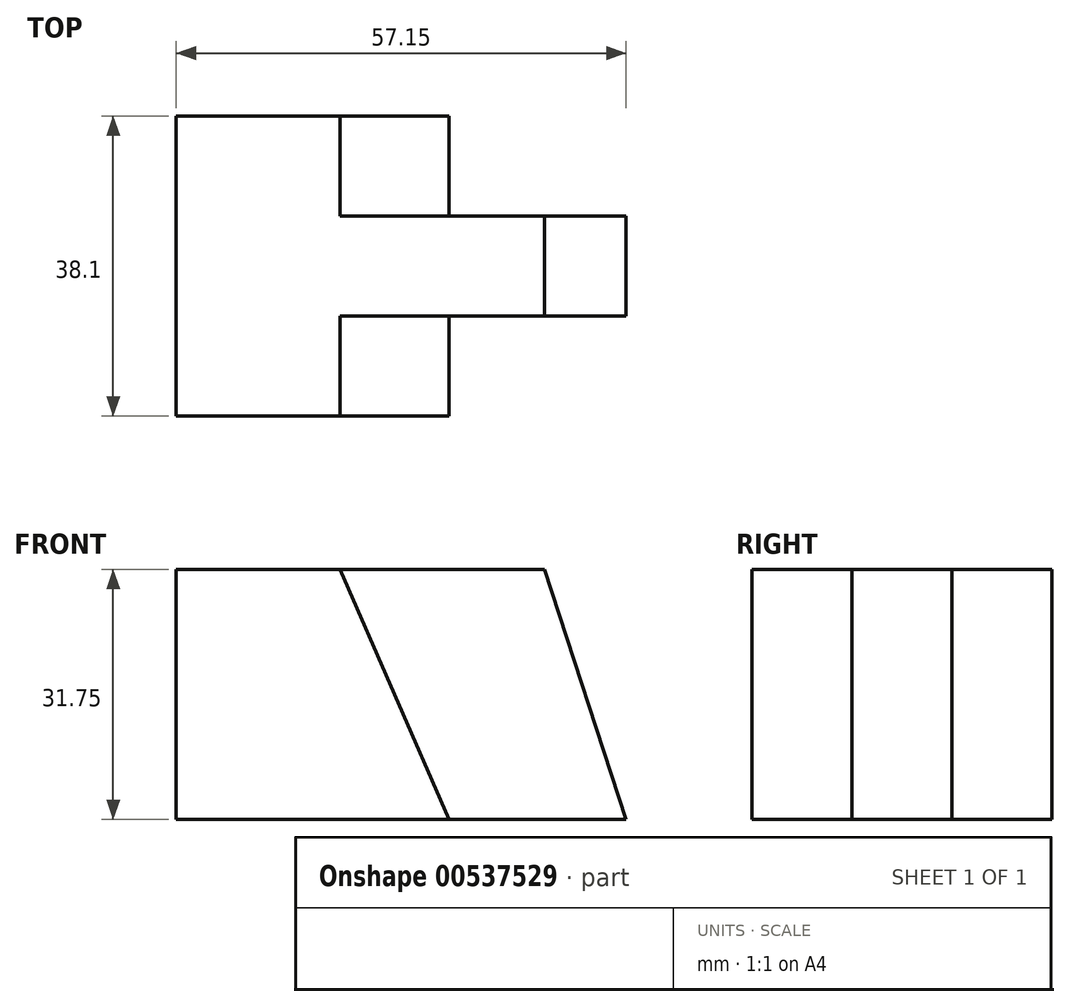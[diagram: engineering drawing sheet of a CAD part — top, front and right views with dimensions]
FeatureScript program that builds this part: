
annotation { "Feature Type Name" : "Feature", "Feature Type Description" : "" }
export const myFeature = defineFeature(function(context is Context, id is Id, definition is map)
    precondition{}
    {
        {
            var Q0;
            Q0=qCreatedBy(makeId("Front.planeOp"),FACE);
            var sketch = newSketch(context, id + "F0", { "sketchPlane" : qUnion([Q0])});
            skLineSegment(sketch, "E0", {"start": v(0, 0) * mm, "end": v(57.15, 0) * mm});
            skLineSegment(sketch, "E1", {"start": v(57.15, 0) * mm, "end": v(57.15, 31.75) * mm});
            skLineSegment(sketch, "E2", {"start": v(57.15, 31.75) * mm, "end": v(0, 31.75) * mm});
            skLineSegment(sketch, "E3", {"start": v(0, 31.75) * mm, "end": v(0, 0) * mm});
            skSolve(sketch);
        }
        {
            var Q0;
            Q0=makeQuery(id+"F0.imprint","IMPRINT",FACE,{"disambiguationData":[TD([[makeQuery(id+"F0.imprint","IMPRINT",EDGE,{"derivedFrom":sQuery(id+"F0.wireOp",EDGE,"E0")}),1.0]])]});
            extrude(context, id + "F1", {"entities" : qUnion([Q0]), "depth" : 38.1 * mm, "offsetDistance" : 25.4 * mm});
        }
        {
            var Q0;
            Q0=makeQuery(id+"F1.opExtrude","CAP_FACE",FACE,{"disambiguationData":[OSD([sQuery(id+"F0.wireOp",EDGE,"E0"),sQuery(id+"F0.wireOp",EDGE,"E1"),sQuery(id+"F0.wireOp",EDGE,"E2"),sQuery(id+"F0.wireOp",EDGE,"E3")])],"isStart":false});
            var sketch = newSketch(context, id + "F2", { "sketchPlane" : qUnion([Q0])});
            skLineSegment(sketch, "E4", {"start": v(20.79, 31.75) * mm, "end": v(34.64, 0) * mm});
            skSolve(sketch);
        }
        {
            var Q0;
            {var subQ0=sQuery(id+"F2.wireOp",EDGE,"E4");Q0=makeQuery(id+"F2.imprint","IMPRINT",FACE,{"disambiguationData":[TD([[makeQuery(id+"F2.imprint","IMPRINT",EDGE,{"derivedFrom":subQ0}),1.0]])]});}
            extrude(context, id + "F3", {"entities" : qUnion([Q0]), "operationType" : NewBodyOperationType.REMOVE, "oppositeDirection" : true, "depth" : 12.7 * mm, "offsetDistance" : 25.4 * mm});
        }
        {
            var Q0;
            Q0=makeQuery(id+"F1.opExtrude","CAP_FACE",FACE,{"disambiguationData":[OSD([sQuery(id+"F0.wireOp",EDGE,"E0"),sQuery(id+"F0.wireOp",EDGE,"E1"),sQuery(id+"F0.wireOp",EDGE,"E2"),sQuery(id+"F0.wireOp",EDGE,"E3")])],"isStart":true});
            var sketch = newSketch(context, id + "F4", { "sketchPlane" : qUnion([Q0])});
            skLineSegment(sketch, "E5", {"start": v(-20.79, 31.75) * mm, "end": v(-34.64, 0) * mm});
            skSolve(sketch);
        }
        {
            var Q0;
            {var subQ0=sQuery(id+"F4.wireOp",EDGE,"E5");Q0=makeQuery(id+"F4.imprint","IMPRINT",FACE,{"disambiguationData":[TD([[makeQuery(id+"F4.imprint","IMPRINT",EDGE,{"derivedFrom":subQ0}),-1.0]])]});}
            extrude(context, id + "F5", {"entities" : qUnion([Q0]), "operationType" : NewBodyOperationType.REMOVE, "oppositeDirection" : true, "depth" : 12.7 * mm, "offsetDistance" : 25.4 * mm});
        }
        {
            var Q0;
            Q0=makeQuery(id+"F3.boolean.opBoolean","COPY",FACE,{"derivedFrom":makeQuery(id+"F3.opExtrude","CAP_FACE",FACE,{"disambiguationData":[OSD([sQuery(id+"F0.wireOp",EDGE,"E0"),sQuery(id+"F0.wireOp",EDGE,"E1"),sQuery(id+"F0.wireOp",EDGE,"E2"),sQuery(id+"F2.wireOp",EDGE,"E4")])],"isStart":false})});
            var sketch = newSketch(context, id + "F6", { "sketchPlane" : qUnion([Q0])});
            skLineSegment(sketch, "E6", {"start": v(46.77, 31.75) * mm, "end": v(57.15, 0) * mm});
            skSolve(sketch);
        }
        {
            var Q0;
            {var subQ0=sQuery(id+"F6.wireOp",EDGE,"E6");Q0=makeQuery(id+"F6.imprint","IMPRINT",FACE,{"disambiguationData":[TD([[makeQuery(id+"F6.imprint","IMPRINT",EDGE,{"derivedFrom":subQ0}),1.0]])]});}
            extrude(context, id + "F7", {"entities" : qUnion([Q0]), "operationType" : NewBodyOperationType.REMOVE, "oppositeDirection" : true, "depth" : 12.7 * mm, "offsetDistance" : 25.4 * mm});
        }
    });
